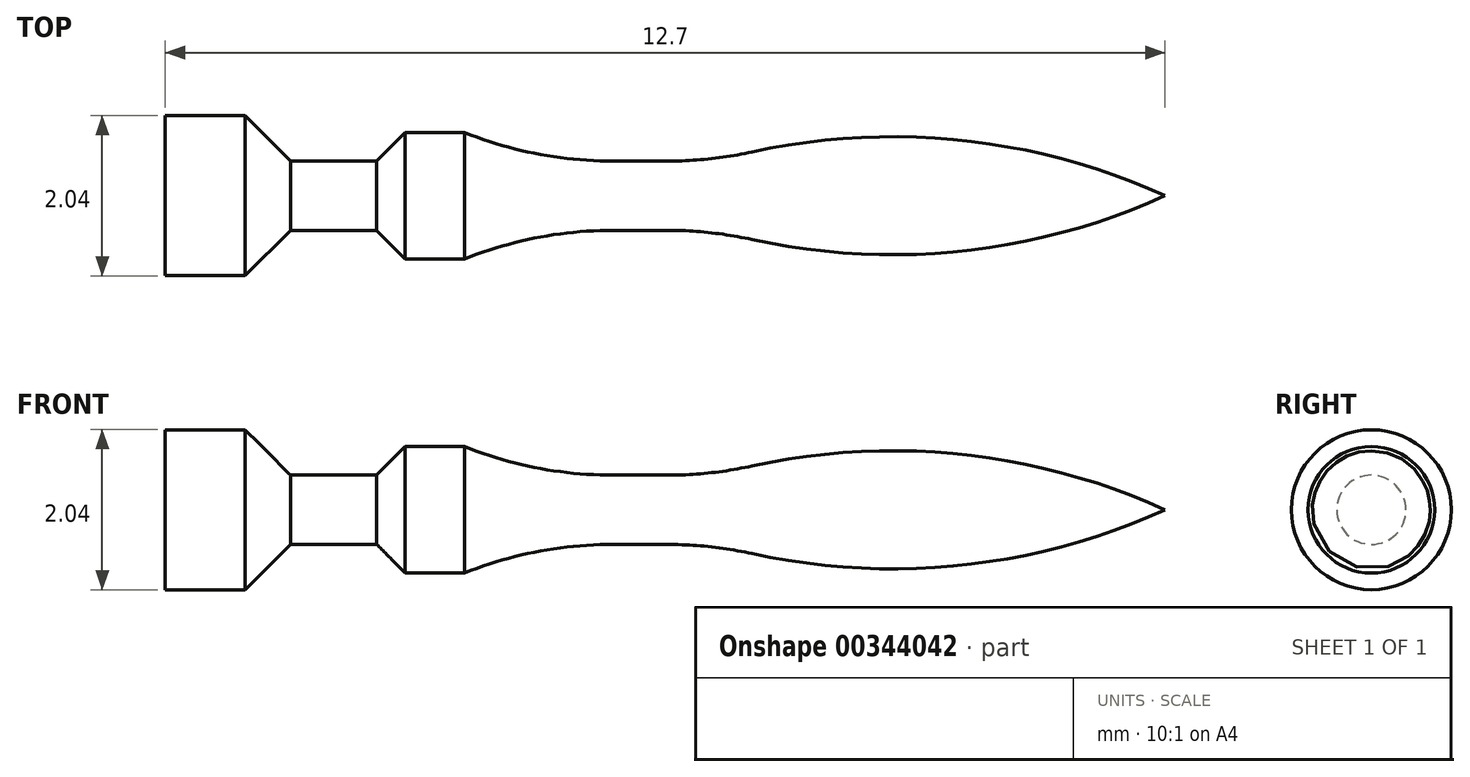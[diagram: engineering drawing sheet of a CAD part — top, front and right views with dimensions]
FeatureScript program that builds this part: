
annotation { "Feature Type Name" : "Feature", "Feature Type Description" : "" }
export const myFeature = defineFeature(function(context is Context, id is Id, definition is map)
    precondition{}
    {
        {
            var Q0;
            Q0=qCreatedBy(makeId("Front.planeOp"),FACE);
            var sketch = newSketch(context, id + "F0", { "sketchPlane" : qUnion([Q0])});
            skLineSegment(sketch, "E0", {"start": v(0, 0) * mm, "end": v(-12.7, 0) * mm});
            skLineSegment(sketch, "E1", {"start": v(-12.7, 0) * mm, "end": v(-12.7, 1.02) * mm});
            skLineSegment(sketch, "E2", {"start": v(-12.7, 1.02) * mm, "end": v(-10.92, 1.02) * mm});
            skLineSegment(sketch, "E3", {"start": v(-10.92, 1.02) * mm, "end": v(-10.92, 0.44) * mm});
            skLineSegment(sketch, "E4", {"start": v(-10.41, 0.44) * mm, "end": v(-10.92, 0.44) * mm});
            skLineSegment(sketch, "E5", {"start": v(-8.9, 0.44) * mm, "end": v(-7.87, 0.44) * mm});
            skLineSegment(sketch, "E6", {"start": v(-7.87, 0.44) * mm, "end": v(-5.72, 0.44) * mm});
            skArc(sketch, "E7", {"start": v(0, 0) * mm, "mid": v(-2.82, 0.73) * mm, "end": v(-5.71, 0.44) * mm});
            skLineSegment(sketch, "E8", {"start": v(-10.41, 0.44) * mm, "end": v(-10.41, 0.8) * mm});
            skLineSegment(sketch, "E9", {"start": v(-10.41, 0.8) * mm, "end": v(-8.9, 0.8) * mm});
            skLineSegment(sketch, "E10", {"start": v(-8.9, 0.8) * mm, "end": v(-8.9, 0.44) * mm});
            skSolve(sketch);
        }
        {
            var Q0;
            Q0=makeQuery(id+"F0.imprint","IMPRINT",FACE,{"disambiguationData":[TD([[makeQuery(id+"F0.imprint","IMPRINT",EDGE,{"derivedFrom":sQuery(id+"F0.wireOp",EDGE,"E0")}),-1.0]])]});
            var Q1;
            Q1=sQuery(id+"F0.wireOp",EDGE,"E0");
            revolve(context, id + "F1", {"entities" : qUnion([Q0]), "axis" : qUnion([Q1]), "revolveType" : RevolveType.FULL});
        }
        {
            var Q0;
            Q0=makeQuery(id+"F1.opRevolve","SWEPT_FACE",FACE,{"disambiguationData":[OSD([sQuery(id+"F0.wireOp",EDGE,"E5"),sQuery(id+"F0.wireOp",EDGE,"E6")])]});
            fillet(context, id + "F2", {"entities" : qUnion([Q0]), "radius" : 5.08 * mm, "tangentPropagation" : true, "allowEdgeOverflow" : false});
        }
        {
            var Q0;
            Q0=makeQuery(id+"F1.opRevolve","SWEPT_EDGE",EDGE,{"disambiguationData":[OSD([sQuery(id+"F0.wireOp",EDGE,"E2"),sQuery(id+"F0.wireOp",EDGE,"E3")])]});
            var Q1;
            Q1=makeQuery(id+"F1.opRevolve","SWEPT_EDGE",EDGE,{"disambiguationData":[OSD([sQuery(id+"F0.wireOp",EDGE,"E8"),sQuery(id+"F0.wireOp",EDGE,"E9")])]});
            chamfer(context, id + "F3", {"entities" : qUnion([Q0, Q1]), "width" : 0.76 * mm, "tangentPropagation" : true});
        }
    });
